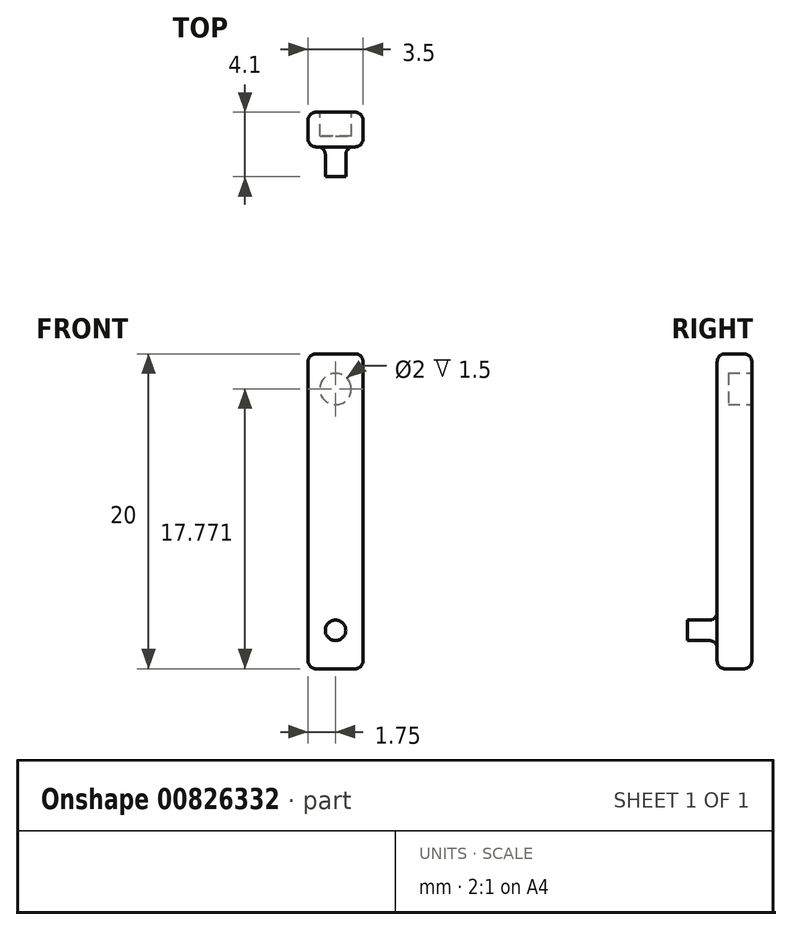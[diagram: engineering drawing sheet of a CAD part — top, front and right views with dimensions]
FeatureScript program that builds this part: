
annotation { "Feature Type Name" : "Feature", "Feature Type Description" : "" }
export const myFeature = defineFeature(function(context is Context, id is Id, definition is map)
    precondition{}
    {
        {
            var Q0;
            Q0=qCreatedBy(makeId("Front.planeOp"),FACE);
            var sketch = newSketch(context, id + "F0", { "sketchPlane" : qUnion([Q0])});
            skLineSegment(sketch, "E0.bottom", {"start": v(1.75, -10) * mm, "end": v(-1.75, -10) * mm});
            skLineSegment(sketch, "E0.top", {"start": v(1.75, 10) * mm, "end": v(-1.75, 10) * mm});
            skLineSegment(sketch, "E0.left", {"start": v(1.75, -10) * mm, "end": v(1.75, 10) * mm});
            skLineSegment(sketch, "E0.right", {"start": v(-1.75, -10) * mm, "end": v(-1.75, 10) * mm});
            skPoint(sketch, "E0.middle", {"position": v(0, 0) * mm});
            skSolve(sketch);
        }
        {
            var Q0;
            Q0=makeQuery(id+"F0.imprint","IMPRINT",FACE,{"disambiguationData":[TD([[makeQuery(id+"F0.imprint","IMPRINT",EDGE,{"derivedFrom":sQuery(id+"F0.wireOp",EDGE,"E0.bottom")}),-1.0]])]});
            extrude(context, id + "F1", {"entities" : qUnion([Q0]), "depth" : 2.2 * mm, "offsetDistance" : 25 * mm});
        }
        {
            var Q0;
            Q0=makeQuery(id+"F1.opExtrude","CAP_FACE",FACE,{"disambiguationData":[OSD([sQuery(id+"F0.wireOp",EDGE,"E0.bottom"),sQuery(id+"F0.wireOp",EDGE,"E0.top"),sQuery(id+"F0.wireOp",EDGE,"E0.left"),sQuery(id+"F0.wireOp",EDGE,"E0.right")])],"isStart":true});
            var sketch = newSketch(context, id + "F2", { "sketchPlane" : qUnion([Q0])});
            skCircle(sketch, "E1", {"center": v(0, 7.77) * mm, "radius": 1 * mm});
            skSolve(sketch);
        }
        {
            var Q0;
            Q0=makeQuery(id+"F2.imprint","IMPRINT",FACE,{"disambiguationData":[TD([[makeQuery(id+"F2.imprint","IMPRINT",EDGE,{"derivedFrom":sQuery(id+"F2.wireOp",EDGE,"E1")}),1.0]])]});
            extrude(context, id + "F3", {"entities" : qUnion([Q0]), "operationType" : NewBodyOperationType.REMOVE, "oppositeDirection" : true, "depth" : 1.5 * mm, "offsetDistance" : 25 * mm});
        }
        {
            var Q0;
            Q0=makeQuery(id+"F1.opExtrude","CAP_FACE",FACE,{"disambiguationData":[OSD([sQuery(id+"F0.wireOp",EDGE,"E0.bottom"),sQuery(id+"F0.wireOp",EDGE,"E0.top"),sQuery(id+"F0.wireOp",EDGE,"E0.left"),sQuery(id+"F0.wireOp",EDGE,"E0.right")])],"isStart":false});
            var sketch = newSketch(context, id + "F4", { "sketchPlane" : qUnion([Q0])});
            skCircle(sketch, "E2", {"center": v(0, -7.56) * mm, "radius": 0.65 * mm});
            skSolve(sketch);
        }
        {
            var Q0;
            Q0=makeQuery(id+"F4.imprint","IMPRINT",FACE,{"disambiguationData":[TD([[makeQuery(id+"F4.imprint","IMPRINT",EDGE,{"derivedFrom":sQuery(id+"F4.wireOp",EDGE,"E2")}),1.0]])]});
            extrude(context, id + "F5", {"entities" : qUnion([Q0]), "operationType" : NewBodyOperationType.ADD, "depth" : 1.9 * mm, "offsetDistance" : 25 * mm});
        }
        {
            var Q0;
            Q0=makeQuery(id+"F1.opExtrude","SWEPT_FACE",FACE,{"disambiguationData":[OSD([sQuery(id+"F0.wireOp",EDGE,"E0.left")])]});
            var Q1;
            Q1=makeQuery(id+"F1.opExtrude","CAP_FACE",FACE,{"disambiguationData":[OSD([sQuery(id+"F0.wireOp",EDGE,"E0.bottom"),sQuery(id+"F0.wireOp",EDGE,"E0.top"),sQuery(id+"F0.wireOp",EDGE,"E0.left"),sQuery(id+"F0.wireOp",EDGE,"E0.right")])],"isStart":false});
            var Q2;
            Q2=makeQuery(id+"F1.opExtrude","SWEPT_FACE",FACE,{"disambiguationData":[OSD([sQuery(id+"F0.wireOp",EDGE,"E0.right")])]});
            var Q3;
            Q3=makeQuery(id+"F1.opExtrude","SWEPT_FACE",FACE,{"disambiguationData":[OSD([sQuery(id+"F0.wireOp",EDGE,"E0.top")])]});
            var Q4;
            Q4=makeQuery(id+"F1.opExtrude","SWEPT_FACE",FACE,{"disambiguationData":[OSD([sQuery(id+"F0.wireOp",EDGE,"E0.bottom")])]});
            fillet(context, id + "F6", {"entities" : qUnion([Q0, Q1, Q2, Q3, Q4]), "radius" : 0.5 * mm, "tangentPropagation" : true, "allowEdgeOverflow" : false});
        }
    });
